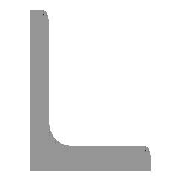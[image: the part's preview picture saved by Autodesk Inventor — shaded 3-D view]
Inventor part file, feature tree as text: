
AUTODESK INVENTOR PART (.ipt)
format: ipt  version: 2013 (Build 170138000, 138)  size: 129,024 bytes
history: native  units: mm (DEFAULTED — no unit token found)
features: other x4, plane x3, split x2, sketch x2
ambient origin geometry x8: Origin, YZ Plane, XZ Plane, XY Plane, X Axis, Y Axis, Z Axis, Center Point
bodies: Solid1 (feature_tree), Body (feature_tree)
feature tree (11):
  parser-record x1  (decoder bookkeeping rows leaked as tree rows — omitted from the tree; the rows remain in map.json)
  other  "Driven Length"
  other  "Start plane"
  other  "End plane"
  plane  "Work Plane4"
  split  "Split1"
  plane  "Work Plane5"
  split  "Split2"
  sketch  "Sketch3"  dims[d0=38.1mm]
  plane  "Work Plane3"
  sketch  "Sketch4"  dims[d1=38.1mm d2=4.7625mm d3=4.7625mm d4=1263.65mm d5=0.0mm d10=0.0mm d11=0.0mm d12=-0.0mm d13=1263.65mm d14=4.826mm d15=2.286mm d16=90.0deg d17=1263.65mm]
